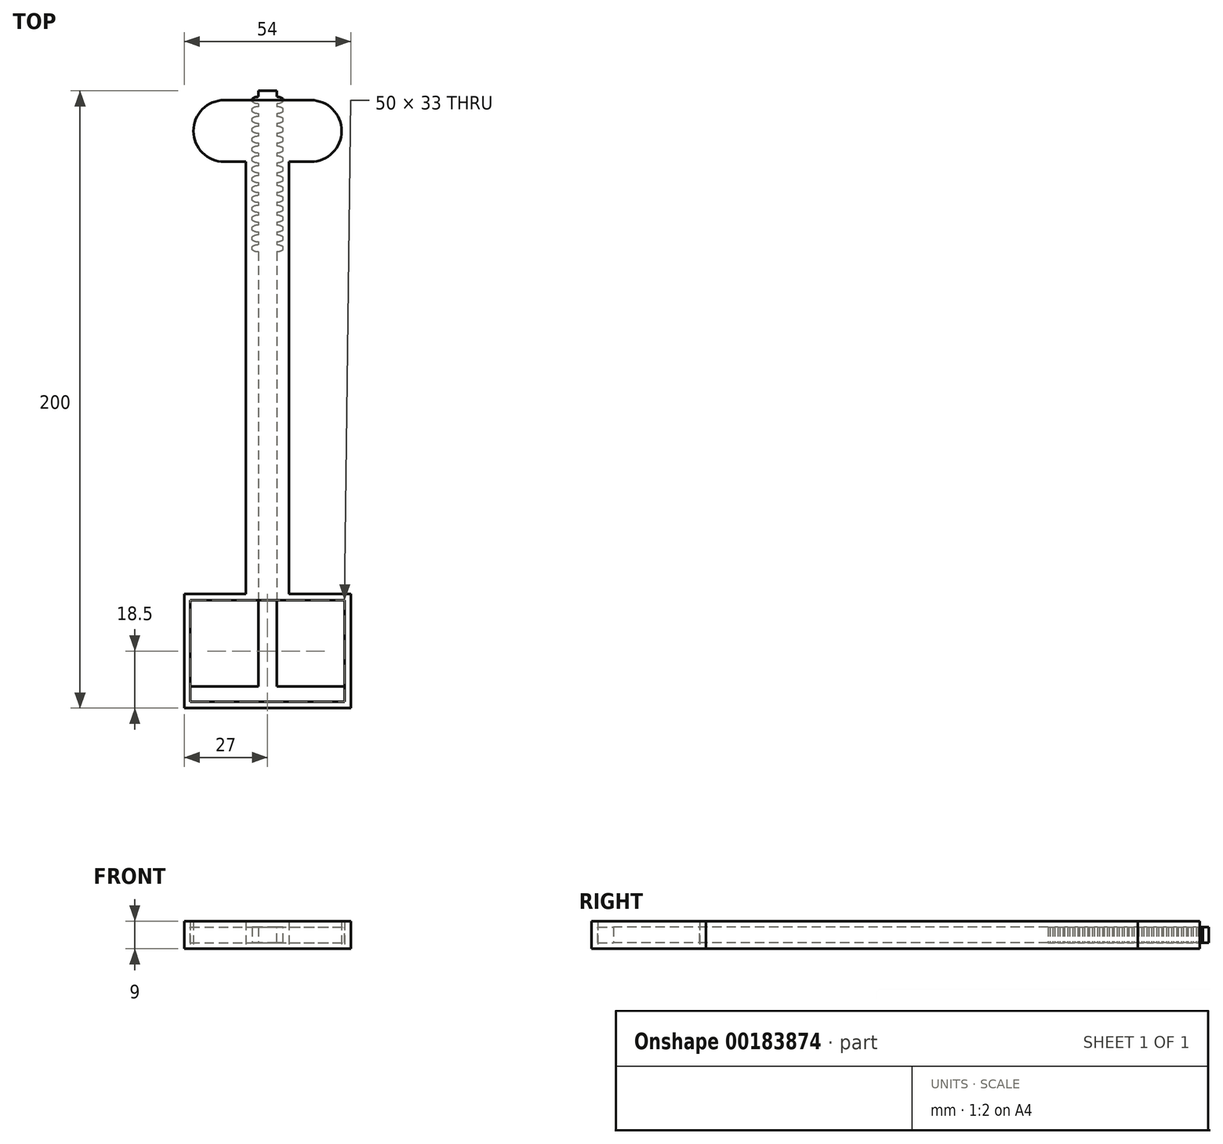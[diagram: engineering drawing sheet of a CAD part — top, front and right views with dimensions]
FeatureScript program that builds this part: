
annotation { "Feature Type Name" : "Feature", "Feature Type Description" : "" }
export const myFeature = defineFeature(function(context is Context, id is Id, definition is map)
    precondition{}
    {
        {
            var Q0;
            Q0=qCreatedBy(makeId("Top.planeOp"),FACE);
            var sketch = newSketch(context, id + "F0", { "sketchPlane" : qUnion([Q0])});
            skLineSegment(sketch, "E0.bottom", {"start": v(0, 13) * mm, "end": v(3, 13) * mm});
            skLineSegment(sketch, "E0.top", {"start": v(0, -180) * mm, "end": v(3, -180) * mm});
            skLineSegment(sketch, "E0.left", {"start": v(0, 13) * mm, "end": v(0, -180) * mm});
            skLineSegment(sketch, "E0.right", {"start": v(3, 13) * mm, "end": v(3, -180) * mm});
            skLineSegment(sketch, "E1", {"start": v(0, 10) * mm, "end": v(3, 10) * mm, "construction": true});
            skArc(sketch, "E2", {"start": v(3, 11.09) * mm, "mid": v(4.04, 10.94) * mm, "end": v(5, 10.5) * mm});
            skLineSegment(sketch, "E3", {"start": v(5, 10.5) * mm, "end": v(5, 10) * mm});
            skArc(sketch, "E4.MirrorCS", {"start": v(3, 8.91) * mm, "mid": v(4.04, 9.06) * mm, "end": v(5, 9.5) * mm});
            skLineSegment(sketch, "E5.MirrorCS", {"start": v(5, 9.5) * mm, "end": v(5, 10) * mm});
            skArc(sketch, "E6.1.0.0", {"start": v(3, 7.89) * mm, "mid": v(4.04, 7.74) * mm, "end": v(5, 7.3) * mm});
            skLineSegment(sketch, "E6.1.0.1", {"start": v(5, 7.3) * mm, "end": v(5, 6.8) * mm});
            skLineSegment(sketch, "E6.1.0.2", {"start": v(5, 6.3) * mm, "end": v(5, 6.8) * mm});
            skArc(sketch, "E6.1.0.3", {"start": v(3, 5.71) * mm, "mid": v(4.04, 5.86) * mm, "end": v(5, 6.3) * mm});
            skArc(sketch, "E6.2.0.0", {"start": v(3, 4.69) * mm, "mid": v(4.04, 4.54) * mm, "end": v(5, 4.1) * mm});
            skLineSegment(sketch, "E6.2.0.1", {"start": v(5, 4.1) * mm, "end": v(5, 3.6) * mm});
            skLineSegment(sketch, "E6.2.0.2", {"start": v(5, 3.1) * mm, "end": v(5, 3.6) * mm});
            skArc(sketch, "E6.2.0.3", {"start": v(3, 2.51) * mm, "mid": v(4.04, 2.66) * mm, "end": v(5, 3.1) * mm});
            skLineSegment(sketch, "E6.direction1", {"start": v(3, 7.39) * mm, "end": v(3, 4.19) * mm, "construction": true});
            skArc(sketch, "E7.0.3.0", {"start": v(3, 1.49) * mm, "mid": v(4.04, 1.34) * mm, "end": v(5, 0.9) * mm});
            skLineSegment(sketch, "E7.4.3.0", {"start": v(5, 0.9) * mm, "end": v(5, 0.4) * mm});
            skLineSegment(sketch, "E7.7.3.0", {"start": v(5, -0.1) * mm, "end": v(5, 0.4) * mm});
            skArc(sketch, "E7.10.3.0", {"start": v(3, -0.69) * mm, "mid": v(4.04, -0.54) * mm, "end": v(5, -0.1) * mm});
            skArc(sketch, "E7.0.4.0", {"start": v(3, -1.71) * mm, "mid": v(4.04, -1.86) * mm, "end": v(5, -2.3) * mm});
            skLineSegment(sketch, "E7.4.4.0", {"start": v(5, -2.3) * mm, "end": v(5, -2.8) * mm});
            skLineSegment(sketch, "E7.7.4.0", {"start": v(5, -3.3) * mm, "end": v(5, -2.8) * mm});
            skArc(sketch, "E7.10.4.0", {"start": v(3, -3.89) * mm, "mid": v(4.04, -3.74) * mm, "end": v(5, -3.3) * mm});
            skArc(sketch, "E7.0.5.0", {"start": v(3, -4.91) * mm, "mid": v(4.04, -5.06) * mm, "end": v(5, -5.5) * mm});
            skLineSegment(sketch, "E7.4.5.0", {"start": v(5, -5.5) * mm, "end": v(5, -6) * mm});
            skLineSegment(sketch, "E7.7.5.0", {"start": v(5, -6.5) * mm, "end": v(5, -6) * mm});
            skArc(sketch, "E7.10.5.0", {"start": v(3, -7.09) * mm, "mid": v(4.04, -6.94) * mm, "end": v(5, -6.5) * mm});
            skArc(sketch, "E7.0.6.0", {"start": v(3, -8.11) * mm, "mid": v(4.04, -8.26) * mm, "end": v(5, -8.7) * mm});
            skLineSegment(sketch, "E7.4.6.0", {"start": v(5, -8.7) * mm, "end": v(5, -9.2) * mm});
            skLineSegment(sketch, "E7.7.6.0", {"start": v(5, -9.7) * mm, "end": v(5, -9.2) * mm});
            skArc(sketch, "E7.10.6.0", {"start": v(3, -10.29) * mm, "mid": v(4.04, -10.14) * mm, "end": v(5, -9.7) * mm});
            skArc(sketch, "E7.0.7.0", {"start": v(3, -11.31) * mm, "mid": v(4.04, -11.46) * mm, "end": v(5, -11.9) * mm});
            skLineSegment(sketch, "E7.4.7.0", {"start": v(5, -11.9) * mm, "end": v(5, -12.4) * mm});
            skLineSegment(sketch, "E7.7.7.0", {"start": v(5, -12.9) * mm, "end": v(5, -12.4) * mm});
            skArc(sketch, "E7.10.7.0", {"start": v(3, -13.49) * mm, "mid": v(4.04, -13.34) * mm, "end": v(5, -12.9) * mm});
            skArc(sketch, "E7.0.8.0", {"start": v(3, -14.51) * mm, "mid": v(4.04, -14.66) * mm, "end": v(5, -15.1) * mm});
            skLineSegment(sketch, "E7.4.8.0", {"start": v(5, -15.1) * mm, "end": v(5, -15.6) * mm});
            skLineSegment(sketch, "E7.7.8.0", {"start": v(5, -16.1) * mm, "end": v(5, -15.6) * mm});
            skArc(sketch, "E7.10.8.0", {"start": v(3, -16.69) * mm, "mid": v(4.04, -16.54) * mm, "end": v(5, -16.1) * mm});
            skArc(sketch, "E7.0.9.0", {"start": v(3, -17.71) * mm, "mid": v(4.04, -17.86) * mm, "end": v(5, -18.3) * mm});
            skLineSegment(sketch, "E7.4.9.0", {"start": v(5, -18.3) * mm, "end": v(5, -18.8) * mm});
            skLineSegment(sketch, "E7.7.9.0", {"start": v(5, -19.3) * mm, "end": v(5, -18.8) * mm});
            skArc(sketch, "E7.10.9.0", {"start": v(3, -19.89) * mm, "mid": v(4.04, -19.74) * mm, "end": v(5, -19.3) * mm});
            skArc(sketch, "E7.0.10.0", {"start": v(3, -20.91) * mm, "mid": v(4.04, -21.06) * mm, "end": v(5, -21.5) * mm});
            skLineSegment(sketch, "E7.4.10.0", {"start": v(5, -21.5) * mm, "end": v(5, -22) * mm});
            skLineSegment(sketch, "E7.7.10.0", {"start": v(5, -22.5) * mm, "end": v(5, -22) * mm});
            skArc(sketch, "E7.10.10.0", {"start": v(3, -23.09) * mm, "mid": v(4.04, -22.94) * mm, "end": v(5, -22.5) * mm});
            skArc(sketch, "E7.0.11.0", {"start": v(3, -24.11) * mm, "mid": v(4.04, -24.26) * mm, "end": v(5, -24.7) * mm});
            skLineSegment(sketch, "E7.4.11.0", {"start": v(5, -24.7) * mm, "end": v(5, -25.2) * mm});
            skLineSegment(sketch, "E7.7.11.0", {"start": v(5, -25.7) * mm, "end": v(5, -25.2) * mm});
            skArc(sketch, "E7.10.11.0", {"start": v(3, -26.29) * mm, "mid": v(4.04, -26.14) * mm, "end": v(5, -25.7) * mm});
            skArc(sketch, "E7.0.12.0", {"start": v(3, -27.31) * mm, "mid": v(4.04, -27.46) * mm, "end": v(5, -27.9) * mm});
            skLineSegment(sketch, "E7.4.12.0", {"start": v(5, -27.9) * mm, "end": v(5, -28.4) * mm});
            skLineSegment(sketch, "E7.7.12.0", {"start": v(5, -28.9) * mm, "end": v(5, -28.4) * mm});
            skArc(sketch, "E7.10.12.0", {"start": v(3, -29.49) * mm, "mid": v(4.04, -29.34) * mm, "end": v(5, -28.9) * mm});
            skArc(sketch, "E7.0.13.0", {"start": v(3, -30.51) * mm, "mid": v(4.04, -30.66) * mm, "end": v(5, -31.1) * mm});
            skLineSegment(sketch, "E7.4.13.0", {"start": v(5, -31.1) * mm, "end": v(5, -31.6) * mm});
            skLineSegment(sketch, "E7.7.13.0", {"start": v(5, -32.1) * mm, "end": v(5, -31.6) * mm});
            skArc(sketch, "E7.10.13.0", {"start": v(3, -32.69) * mm, "mid": v(4.04, -32.54) * mm, "end": v(5, -32.1) * mm});
            skArc(sketch, "E7.0.14.0", {"start": v(3, -33.71) * mm, "mid": v(4.04, -33.86) * mm, "end": v(5, -34.3) * mm});
            skLineSegment(sketch, "E7.4.14.0", {"start": v(5, -34.3) * mm, "end": v(5, -34.8) * mm});
            skLineSegment(sketch, "E7.7.14.0", {"start": v(5, -35.3) * mm, "end": v(5, -34.8) * mm});
            skArc(sketch, "E7.10.14.0", {"start": v(3, -35.89) * mm, "mid": v(4.04, -35.74) * mm, "end": v(5, -35.3) * mm});
            skArc(sketch, "E7.0.15.0", {"start": v(3, -36.91) * mm, "mid": v(4.04, -37.06) * mm, "end": v(5, -37.5) * mm});
            skLineSegment(sketch, "E7.4.15.0", {"start": v(5, -37.5) * mm, "end": v(5, -38) * mm});
            skLineSegment(sketch, "E7.7.15.0", {"start": v(5, -38.5) * mm, "end": v(5, -38) * mm});
            skArc(sketch, "E7.10.15.0", {"start": v(3, -39.09) * mm, "mid": v(4.04, -38.94) * mm, "end": v(5, -38.5) * mm});
            skSolve(sketch);
        }
        {
            var Q0;
            Q0 = qSketchRegion(id + "F0", true);
            extrude(context, id + "F1", {"entities" : qUnion([Q0]), "depth" : 5 * mm});
        }
        {
            var Q0;
            Q0=makeQuery(id+"F1.opExtrude","SWEPT_BODY",BODY,{"disambiguationData":[OSD([sQuery(id+"F0.wireOp",EDGE,"E0.bottom"),sQuery(id+"F0.wireOp",EDGE,"E0.top"),sQuery(id+"F0.wireOp",EDGE,"E0.left"),sQuery(id+"F0.wireOp",EDGE,"E0.right"),sQuery(id+"F0.wireOp",EDGE,"E2"),sQuery(id+"F0.wireOp",EDGE,"E3"),sQuery(id+"F0.wireOp",EDGE,"E4.MirrorCS"),sQuery(id+"F0.wireOp",EDGE,"E5.MirrorCS"),sQuery(id+"F0.wireOp",EDGE,"E6.1.0.0"),sQuery(id+"F0.wireOp",EDGE,"E6.1.0.1"),sQuery(id+"F0.wireOp",EDGE,"E6.1.0.2"),sQuery(id+"F0.wireOp",EDGE,"E6.1.0.3"),sQuery(id+"F0.wireOp",EDGE,"E6.2.0.0"),sQuery(id+"F0.wireOp",EDGE,"E6.2.0.1"),sQuery(id+"F0.wireOp",EDGE,"E6.2.0.2"),sQuery(id+"F0.wireOp",EDGE,"E6.2.0.3"),sQuery(id+"F0.wireOp",EDGE,"E7.0.3.0"),sQuery(id+"F0.wireOp",EDGE,"E7.4.3.0"),sQuery(id+"F0.wireOp",EDGE,"E7.7.3.0"),sQuery(id+"F0.wireOp",EDGE,"E7.10.3.0"),sQuery(id+"F0.wireOp",EDGE,"E7.0.4.0"),sQuery(id+"F0.wireOp",EDGE,"E7.4.4.0"),sQuery(id+"F0.wireOp",EDGE,"E7.7.4.0"),sQuery(id+"F0.wireOp",EDGE,"E7.10.4.0"),sQuery(id+"F0.wireOp",EDGE,"E7.0.5.0"),sQuery(id+"F0.wireOp",EDGE,"E7.4.5.0"),sQuery(id+"F0.wireOp",EDGE,"E7.7.5.0"),sQuery(id+"F0.wireOp",EDGE,"E7.10.5.0"),sQuery(id+"F0.wireOp",EDGE,"E7.0.6.0"),sQuery(id+"F0.wireOp",EDGE,"E7.4.6.0"),sQuery(id+"F0.wireOp",EDGE,"E7.7.6.0"),sQuery(id+"F0.wireOp",EDGE,"E7.10.6.0"),sQuery(id+"F0.wireOp",EDGE,"E7.0.7.0"),sQuery(id+"F0.wireOp",EDGE,"E7.4.7.0"),sQuery(id+"F0.wireOp",EDGE,"E7.7.7.0"),sQuery(id+"F0.wireOp",EDGE,"E7.10.7.0"),sQuery(id+"F0.wireOp",EDGE,"E7.0.8.0"),sQuery(id+"F0.wireOp",EDGE,"E7.4.8.0"),sQuery(id+"F0.wireOp",EDGE,"E7.7.8.0"),sQuery(id+"F0.wireOp",EDGE,"E7.10.8.0"),sQuery(id+"F0.wireOp",EDGE,"E7.0.9.0"),sQuery(id+"F0.wireOp",EDGE,"E7.4.9.0"),sQuery(id+"F0.wireOp",EDGE,"E7.7.9.0"),sQuery(id+"F0.wireOp",EDGE,"E7.10.9.0"),sQuery(id+"F0.wireOp",EDGE,"E7.0.10.0"),sQuery(id+"F0.wireOp",EDGE,"E7.4.10.0"),sQuery(id+"F0.wireOp",EDGE,"E7.7.10.0"),sQuery(id+"F0.wireOp",EDGE,"E7.10.10.0"),sQuery(id+"F0.wireOp",EDGE,"E7.0.11.0"),sQuery(id+"F0.wireOp",EDGE,"E7.4.11.0"),sQuery(id+"F0.wireOp",EDGE,"E7.7.11.0"),sQuery(id+"F0.wireOp",EDGE,"E7.10.11.0"),sQuery(id+"F0.wireOp",EDGE,"E7.0.12.0"),sQuery(id+"F0.wireOp",EDGE,"E7.4.12.0"),sQuery(id+"F0.wireOp",EDGE,"E7.7.12.0"),sQuery(id+"F0.wireOp",EDGE,"E7.10.12.0"),sQuery(id+"F0.wireOp",EDGE,"E7.0.13.0"),sQuery(id+"F0.wireOp",EDGE,"E7.4.13.0"),sQuery(id+"F0.wireOp",EDGE,"E7.7.13.0"),sQuery(id+"F0.wireOp",EDGE,"E7.10.13.0"),sQuery(id+"F0.wireOp",EDGE,"E7.0.14.0"),sQuery(id+"F0.wireOp",EDGE,"E7.4.14.0"),sQuery(id+"F0.wireOp",EDGE,"E7.7.14.0"),sQuery(id+"F0.wireOp",EDGE,"E7.10.14.0"),sQuery(id+"F0.wireOp",EDGE,"E7.0.15.0"),sQuery(id+"F0.wireOp",EDGE,"E7.4.15.0"),sQuery(id+"F0.wireOp",EDGE,"E7.7.15.0"),sQuery(id+"F0.wireOp",EDGE,"E7.10.15.0")])]});
            var Q1;
            Q1=makeQuery(id+"F1.opExtrude","SWEPT_FACE",FACE,{"disambiguationData":[OSD([sQuery(id+"F0.wireOp",EDGE,"E0.left")])]});
            mirror(context, id + "F2", {"operationType" : NewBodyOperationType.ADD, "entities" : qUnion([Q0]), "mirrorPlane" : qUnion([Q1])});
        }
        {
            var Q0;
            {var subQ0=makeQuery(id+"F1.opExtrude","SWEPT_FACE",FACE,{"disambiguationData":[OSD([sQuery(id+"F0.wireOp",EDGE,"E0.top")])]});Q0=makeQuery(id+"F2.boolean.opBoolean","MERGE",FACE,{"derivedFrom":[subQ0,makeQuery(id+"F2.opPattern","COPY",FACE,{"derivedFrom":subQ0,"instanceName":"1"})]});}
            var sketch = newSketch(context, id + "F3", { "sketchPlane" : qUnion([Q0])});
            skLineSegment(sketch, "E8.bottom", {"start": v(-25, 0) * mm, "end": v(25, 0) * mm});
            skLineSegment(sketch, "E8.top", {"start": v(-25, 5) * mm, "end": v(25, 5) * mm});
            skLineSegment(sketch, "E8.left", {"start": v(-25, 0) * mm, "end": v(-25, 5) * mm});
            skLineSegment(sketch, "E8.right", {"start": v(25, 0) * mm, "end": v(25, 5) * mm});
            skPoint(sketch, "E8.middle", {"position": v(0, 2.5) * mm});
            skPoint(sketch, "E8.middle.positionSnap0", {"position": v(-3, 2.5) * mm});
            skPoint(sketch, "E8.centerSnap0", {"position": v(-3, 2.5) * mm});
            skSolve(sketch);
        }
        {
            var Q0;
            Q0 = qSketchRegion(id + "F3", true);
            extrude(context, id + "F4", {"entities" : qUnion([Q0]), "operationType" : NewBodyOperationType.ADD, "depth" : 5 * mm});
        }
        {
            var Q0;
            Q0=qCreatedBy(makeId("Top.planeOp"),FACE);
            var sketch = newSketch(context, id + "F5", { "sketchPlane" : qUnion([Q0])});
            skCircle(sketch, "E9", {"center": v(14, 0) * mm, "radius": 10 * mm});
            skLineSegment(sketch, "E10", {"start": v(0, 10) * mm, "end": v(14, 10) * mm});
            skLineSegment(sketch, "E11", {"start": v(14, -10) * mm, "end": v(7, -10) * mm});
            skLineSegment(sketch, "E12", {"start": v(7, -10) * mm, "end": v(7, -150) * mm});
            skLineSegment(sketch, "E13", {"start": v(7, -150) * mm, "end": v(27, -150) * mm});
            skLineSegment(sketch, "E14", {"start": v(27, -150) * mm, "end": v(27, -187) * mm});
            skLineSegment(sketch, "E15", {"start": v(27, -187) * mm, "end": v(0, -187) * mm});
            skLineSegment(sketch, "E16.MirrorCS", {"start": v(0, 10) * mm, "end": v(-14, 10) * mm});
            skCircle(sketch, "E17.MirrorC", {"center": v(-14, 0) * mm, "radius": 10 * mm});
            skLineSegment(sketch, "E18.MirrorCS", {"start": v(-14, -10) * mm, "end": v(-7, -10) * mm});
            skLineSegment(sketch, "E19.MirrorCS", {"start": v(-7, -10) * mm, "end": v(-7, -150) * mm});
            skLineSegment(sketch, "E20.MirrorCS", {"start": v(-27, -150) * mm, "end": v(-27, -187) * mm});
            skLineSegment(sketch, "E21.MirrorCS", {"start": v(-27, -187) * mm, "end": v(0, -187) * mm});
            skLineSegment(sketch, "E22.MirrorCS", {"start": v(-7, -150) * mm, "end": v(-27, -150) * mm});
            skLineSegment(sketch, "E23.bottom", {"start": v(25, -152) * mm, "end": v(-25, -152) * mm});
            skLineSegment(sketch, "E23.top", {"start": v(25, -185) * mm, "end": v(-25, -185) * mm});
            skLineSegment(sketch, "E23.left", {"start": v(25, -152) * mm, "end": v(25, -185) * mm});
            skLineSegment(sketch, "E23.right", {"start": v(-25, -152) * mm, "end": v(-25, -185) * mm});
            skPoint(sketch, "E23.middle", {"position": v(0, -168.5) * mm});
            skSolve(sketch);
        }
        {
            var Q0;
            Q0 = qSketchRegion(id + "F5", true);
            extrude(context, id + "F6", {"entities" : qUnion([Q0]), "depth" : 7 * mm, "hasSecondDirection" : true, "secondDirectionOppositeDirection" : true, "secondDirectionDepth" : 2 * mm});
        }
        {
            var Q0;
            Q0=makeQuery(id+"F1.opExtrude","SWEPT_BODY",BODY,{"disambiguationData":[OSD([sQuery(id+"F0.wireOp",EDGE,"E0.bottom"),sQuery(id+"F0.wireOp",EDGE,"E0.top"),sQuery(id+"F0.wireOp",EDGE,"E0.left"),sQuery(id+"F0.wireOp",EDGE,"E0.right"),sQuery(id+"F0.wireOp",EDGE,"E2"),sQuery(id+"F0.wireOp",EDGE,"E3"),sQuery(id+"F0.wireOp",EDGE,"E4.MirrorCS"),sQuery(id+"F0.wireOp",EDGE,"E5.MirrorCS"),sQuery(id+"F0.wireOp",EDGE,"E6.1.0.0"),sQuery(id+"F0.wireOp",EDGE,"E6.1.0.1"),sQuery(id+"F0.wireOp",EDGE,"E6.1.0.2"),sQuery(id+"F0.wireOp",EDGE,"E6.1.0.3"),sQuery(id+"F0.wireOp",EDGE,"E6.2.0.0"),sQuery(id+"F0.wireOp",EDGE,"E6.2.0.1"),sQuery(id+"F0.wireOp",EDGE,"E6.2.0.2"),sQuery(id+"F0.wireOp",EDGE,"E6.2.0.3"),sQuery(id+"F0.wireOp",EDGE,"E7.0.3.0"),sQuery(id+"F0.wireOp",EDGE,"E7.4.3.0"),sQuery(id+"F0.wireOp",EDGE,"E7.7.3.0"),sQuery(id+"F0.wireOp",EDGE,"E7.10.3.0"),sQuery(id+"F0.wireOp",EDGE,"E7.0.4.0"),sQuery(id+"F0.wireOp",EDGE,"E7.4.4.0"),sQuery(id+"F0.wireOp",EDGE,"E7.7.4.0"),sQuery(id+"F0.wireOp",EDGE,"E7.10.4.0"),sQuery(id+"F0.wireOp",EDGE,"E7.0.5.0"),sQuery(id+"F0.wireOp",EDGE,"E7.4.5.0"),sQuery(id+"F0.wireOp",EDGE,"E7.7.5.0"),sQuery(id+"F0.wireOp",EDGE,"E7.10.5.0"),sQuery(id+"F0.wireOp",EDGE,"E7.0.6.0"),sQuery(id+"F0.wireOp",EDGE,"E7.4.6.0"),sQuery(id+"F0.wireOp",EDGE,"E7.7.6.0"),sQuery(id+"F0.wireOp",EDGE,"E7.10.6.0"),sQuery(id+"F0.wireOp",EDGE,"E7.0.7.0"),sQuery(id+"F0.wireOp",EDGE,"E7.4.7.0"),sQuery(id+"F0.wireOp",EDGE,"E7.7.7.0"),sQuery(id+"F0.wireOp",EDGE,"E7.10.7.0"),sQuery(id+"F0.wireOp",EDGE,"E7.0.8.0"),sQuery(id+"F0.wireOp",EDGE,"E7.4.8.0"),sQuery(id+"F0.wireOp",EDGE,"E7.7.8.0"),sQuery(id+"F0.wireOp",EDGE,"E7.10.8.0"),sQuery(id+"F0.wireOp",EDGE,"E7.0.9.0"),sQuery(id+"F0.wireOp",EDGE,"E7.4.9.0"),sQuery(id+"F0.wireOp",EDGE,"E7.7.9.0"),sQuery(id+"F0.wireOp",EDGE,"E7.10.9.0"),sQuery(id+"F0.wireOp",EDGE,"E7.0.10.0"),sQuery(id+"F0.wireOp",EDGE,"E7.4.10.0"),sQuery(id+"F0.wireOp",EDGE,"E7.7.10.0"),sQuery(id+"F0.wireOp",EDGE,"E7.10.10.0"),sQuery(id+"F0.wireOp",EDGE,"E7.0.11.0"),sQuery(id+"F0.wireOp",EDGE,"E7.4.11.0"),sQuery(id+"F0.wireOp",EDGE,"E7.7.11.0"),sQuery(id+"F0.wireOp",EDGE,"E7.10.11.0"),sQuery(id+"F0.wireOp",EDGE,"E7.0.12.0"),sQuery(id+"F0.wireOp",EDGE,"E7.4.12.0"),sQuery(id+"F0.wireOp",EDGE,"E7.7.12.0"),sQuery(id+"F0.wireOp",EDGE,"E7.10.12.0"),sQuery(id+"F0.wireOp",EDGE,"E7.0.13.0"),sQuery(id+"F0.wireOp",EDGE,"E7.4.13.0"),sQuery(id+"F0.wireOp",EDGE,"E7.7.13.0"),sQuery(id+"F0.wireOp",EDGE,"E7.10.13.0"),sQuery(id+"F0.wireOp",EDGE,"E7.0.14.0"),sQuery(id+"F0.wireOp",EDGE,"E7.4.14.0"),sQuery(id+"F0.wireOp",EDGE,"E7.7.14.0"),sQuery(id+"F0.wireOp",EDGE,"E7.10.14.0"),sQuery(id+"F0.wireOp",EDGE,"E7.0.15.0"),sQuery(id+"F0.wireOp",EDGE,"E7.4.15.0"),sQuery(id+"F0.wireOp",EDGE,"E7.7.15.0"),sQuery(id+"F0.wireOp",EDGE,"E7.10.15.0")])]});
            var Q1;
            Q1=makeQuery(id+"F6.opExtrude","SWEPT_BODY",BODY,{"disambiguationData":[OSD([sQuery(id+"F5.wireOp",EDGE,"E9"),sQuery(id+"F5.wireOp",EDGE,"E10"),sQuery(id+"F5.wireOp",EDGE,"E11"),sQuery(id+"F5.wireOp",EDGE,"E12"),sQuery(id+"F5.wireOp",EDGE,"E13"),sQuery(id+"F5.wireOp",EDGE,"E14"),sQuery(id+"F5.wireOp",EDGE,"E15"),sQuery(id+"F5.wireOp",EDGE,"E16.MirrorCS"),sQuery(id+"F5.wireOp",EDGE,"E17.MirrorC"),sQuery(id+"F5.wireOp",EDGE,"E18.MirrorCS"),sQuery(id+"F5.wireOp",EDGE,"E19.MirrorCS"),sQuery(id+"F5.wireOp",EDGE,"E20.MirrorCS"),sQuery(id+"F5.wireOp",EDGE,"E21.MirrorCS"),sQuery(id+"F5.wireOp",EDGE,"E22.MirrorCS"),sQuery(id+"F5.wireOp",EDGE,"E23.bottom"),sQuery(id+"F5.wireOp",EDGE,"E23.top"),sQuery(id+"F5.wireOp",EDGE,"E23.left"),sQuery(id+"F5.wireOp",EDGE,"E23.right")])]});
            booleanBodies(context, id + "F7", {"operationType" : BooleanOperationType.SUBTRACTION, "tools" : qUnion([Q0]), "targets" : qUnion([Q1]), "keepTools" : true});
        }
    });
